# Revit family: IEK_Держатель проводника круглого_8мм_Плоская кровля
name_source: partatom
category: Обобщенные модели
units: mm (PartAtom-declared; Revit-internal decimal feet)

## family parameters
Может служить основой для арматурных стержней = Нет
Общий = Да
Основа = Грань
При загрузке вырезать с полостями = Нет
Размер круглого соединителя = Использовать диаметр
Тип детали = Нормальный
Точка расчета площади = Нет

## types (2) — shared parameters
ADSK_URL страницы изделия = https://www.iek.ru
ADSK_Версия Revit = 2019
ADSK_Версия семейства = 1.0
ADSK_Группирование = VIII. ЭЛЕМЕНТЫ ВНЕШНЕЙ МОЛНИЕЗАЩИТЫ
ADSK_Единица измерения = шт
ADSK_Завод-изготовитель = IEK
ADSK_Материал = RAL 7024 Графитовый серый
IEK_URL = https://www.iek.ru
IEK_Описание = Универсальная конструкция держателя позволяет использовать его с проводниками различной формы и габаритами.
KSI_CMa_Строительные материалы = 01.7.14.03
zero-valued in all types: Отметка по умолчанию

## per-type parameters (varying)
| type | ADSK_Код изделия | ADSK_Масса | ADSK_Материал наименование | ADSK_Наименование | IEK_Цена за единицу |
| 8мм_Пластик с бетоном | ZDP80-70-6-08 | 1 | Пластик с бетоном | Держатель проводника круглого 8мм для плоской кровли пластик с бетоном IEK | 224.95 |
| 8мм_Пластик | ZDP80-60-6-08 | 0.1 | Пластик | Держатель проводника круглого 8мм для плоской кровли пластик IEK | 240 |
